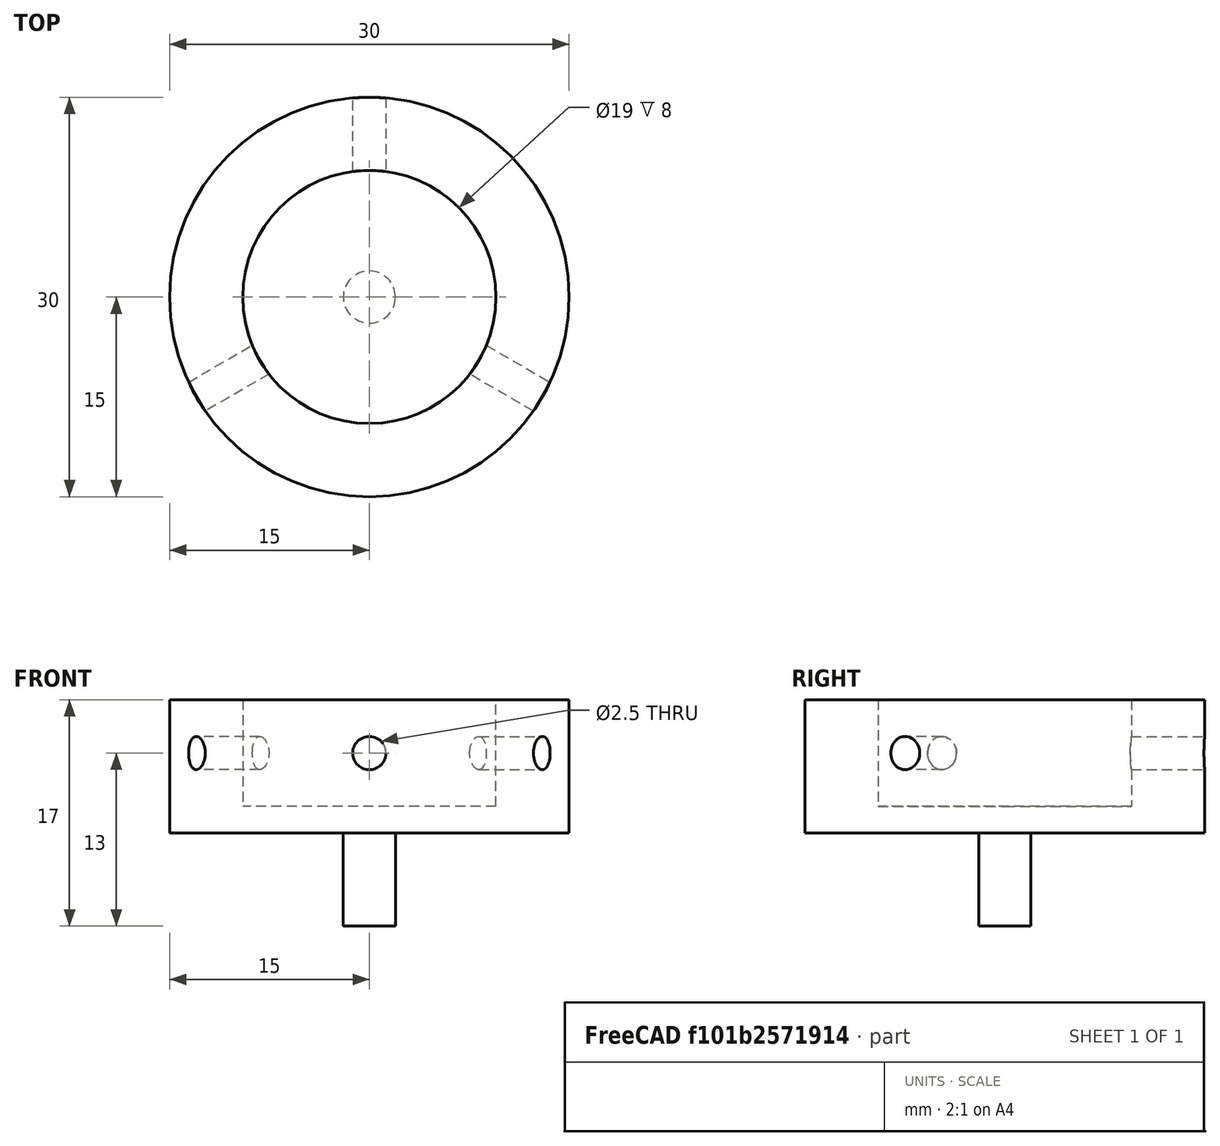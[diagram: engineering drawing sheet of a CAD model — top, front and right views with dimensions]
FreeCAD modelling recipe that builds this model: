
FCSTD DOCUMENT  (FreeCAD 0.20R29603 (Git))
Label: PhilippsXL30_SampleMountAdapter_M4to19mm
License: All rights reserved
LicenseURL: http://en.wikipedia.org/wiki/All_rights_reserved
objects: TechDraw::DrawViewDimension×15, Part::Cylinder×6, TechDraw::DrawProjGroupItem×5, Part::Compound×4, TechDraw::DrawProjGroup×3, Part::Cut×2, TechDraw::DrawViewSection×2, Part::MultiFuse×1, Part::Feature×1, TechDraw::DrawSVGTemplate×1, TechDraw::DrawPage×1
note: 14 computed .brp shape members not serialized (recipe doc carries the construction recipe); baked Part::Feature solids carry a one-line shape summary decoded from their .brp

FEATURE [Part::Cylinder] Cylinder  label="Zylinder"
  Angle = 360
  AttacherType = Attacher::AttachEngine3D
  FirstAngle = 0
  Height = 10
  Radius = 15
  SecondAngle = 0
FEATURE [Part::Cylinder] Cylinder001  label="Zylinder001"
  Angle = 360
  AttacherType = Attacher::AttachEngine3D
  FirstAngle = 0
  Height = 8
  Placement = pos=(0,0,2) rot=(0,0,1;0rad)
  Radius = 9.5
  SecondAngle = 0
FEATURE [Part::Cut] Cut
  Base = -> Cylinder
  Tool = -> Cylinder001
FEATURE [Part::Cylinder] Cylinder002  label="Zylinder002"
  Angle = 360
  AttacherType = Attacher::AttachEngine3D
  FirstAngle = 0
  Height = 6
  Placement = pos=(0,15.2,6) rot=(1,0,0;1.5708rad)
  Radius = 1.25
  SecondAngle = 0
FEATURE [Part::Compound] Compound
  Links = -> [Cylinder002]
FEATURE [Part::Cylinder] Cylinder003  label="Zylinder003"
  Angle = 360
  AttacherType = Attacher::AttachEngine3D
  FirstAngle = 0
  Height = 6
  Placement = pos=(0,15.2,6) rot=(1,0,0;1.5708rad)
  Radius = 1.25
  SecondAngle = 0
FEATURE [Part::Compound] Compound001
  Links = -> [Cylinder003]
  Placement = pos=(0,0,0) rot=(0,0,1;2.0944rad)
FEATURE [Part::Cylinder] Cylinder004  label="Zylinder004"
  Angle = 360
  AttacherType = Attacher::AttachEngine3D
  FirstAngle = 0
  Height = 6
  Placement = pos=(0,15.2,6) rot=(1,0,0;1.5708rad)
  Radius = 1.25
  SecondAngle = 0
FEATURE [Part::Compound] Compound002
  Links = -> [Cylinder004]
  Placement = pos=(0,0,0) rot=(0,0,1;4.18879rad)
FEATURE [Part::Compound] Compound003  label="M3 setscrews"
  Links = -> [Compound,Compound001,Compound002]
FEATURE [Part::Cut] Cut001
  Base = -> Cut
  Tool = -> Compound003
FEATURE [Part::Cylinder] Cylinder005  label="M4 screw"
  Angle = 360
  AttacherType = Attacher::AttachEngine3D
  FirstAngle = 0
  Height = 7
  Placement = pos=(0,0,-7) rot=(0,0,1;0rad)
  Radius = 1.96
  SecondAngle = 0
FEATURE [Part::MultiFuse] Fusion
  Shapes = -> [Cut001,Cylinder005]
FEATURE [Part::Feature] Fusion_solid  label="PhilippsXL30_SampleMountAdapter_M4to19mm"
  shape: bbox 30 x 30 x 17 mm, 10 faces (baked)
FEATURE [TechDraw::DrawSVGTemplate] Template
  EditableTexts = Designed_by_Name=Thomas Spielauer; Drawing_number=1; FC-Date=2023-08-04; FC-SC=mm; FC-SH=1/1; FC-Title=Sample holder Adapter; Subtitle=M4 to 19mm, XL30 ESEM compatible
  Height = 210
  Orientation = 1
  Width = 297
FEATURE [TechDraw::DrawProjGroupItem] ProjItem  label="Top"
  CoarseView = false
  Direction = (0,0,1)
  Focus = 100
  HardHidden = false
  IsoCount = 0
  IsoHidden = false
  IsoVisible = false
  LockPosition = true
  Perspective = false
  Rotation = 0
  RotationVector = (1,0,0)
  ScaleType = 2
  SeamHidden = false
  SeamVisible = true
  SmoothHidden = false
  SmoothVisible = true
  Source = -> [Fusion_solid]
  Type = 0
  X = 0
  XDirection = (1,0,0)
  Y = 0
FEATURE [TechDraw::DrawProjGroupItem] ProjItem003  label="Side"
  CoarseView = false
  Direction = (0,-1,0)
  Focus = 100
  HardHidden = false
  IsoCount = 0
  IsoHidden = false
  IsoVisible = false
  LockPosition = false
  Perspective = false
  Rotation = 0
  RotationVector = (1,0,0)
  ScaleType = 2
  SeamHidden = false
  SeamVisible = true
  SmoothHidden = false
  SmoothVisible = true
  Source = -> [Fusion_solid]
  Type = 5
  X = 0
  XDirection = (1,0,0)
  Y = 52.416
FEATURE [TechDraw::DrawProjGroupItem] ProjItem004  label="Bottom001"
  CoarseView = false
  Direction = (0,0,-1)
  Focus = 100
  HardHidden = false
  IsoCount = 0
  IsoHidden = false
  IsoVisible = false
  LockPosition = false
  Perspective = false
  Rotation = 0
  RotationVector = (1,0,0)
  ScaleType = 2
  SeamHidden = false
  SeamVisible = true
  SmoothHidden = false
  SmoothVisible = true
  Source = -> [Fusion_solid]
  Type = 3
  X = 57.7589
  XDirection = (-1,0,0)
  Y = 0
FEATURE [TechDraw::DrawProjGroup] ProjGroup
  Anchor = -> ProjItem
  AutoDistribute = false
  LockPosition = false
  ProjectionType = 0
  Rotation = 0
  ScaleType = 0
  Source = -> [Fusion_solid]
  Views = -> [ProjItem,ProjItem003,ProjItem004]
  X = 31.0456
  Y = 115.683
  spacingX = 15
  spacingY = 15
FEATURE [TechDraw::DrawViewDimension] Dimension001
  AngleOverride = false
  Arbitrary = false
  ArbitraryTolerances = false
  EqualTolerance = true
  ExtensionAngle = 0
  FormatSpec = %.2w (M4)
  FormatSpecOverTolerance = %+.2w
  FormatSpecUnderTolerance = %+.2w
  Inverted = false
  LineAngle = 0
  LockPosition = false
  MeasureType = 1
  OverTolerance = 0
  References2D = -> [ProjItem003]
  Rotation = 0
  ScaleType = 0
  TheoreticalExact = false
  Type = 0
  UnderTolerance = 0
  X = 14.6767
  Y = -20.2276
FEATURE [TechDraw::DrawViewDimension] Dimension002
  AngleOverride = false
  Arbitrary = false
  ArbitraryTolerances = false
  EqualTolerance = true
  ExtensionAngle = 0
  FormatSpec = %.2w
  FormatSpecOverTolerance = %+.2w
  FormatSpecUnderTolerance = %+.2w
  Inverted = false
  LineAngle = 0
  LockPosition = false
  MeasureType = 1
  OverTolerance = 0
  References2D = -> [ProjItem003]
  Rotation = 0
  ScaleType = 0
  TheoreticalExact = false
  Type = 0
  UnderTolerance = 0
  X = 23.4662
  Y = 14.9409
FEATURE [TechDraw::DrawViewDimension] Dimension003
  AngleOverride = false
  Arbitrary = false
  ArbitraryTolerances = false
  EqualTolerance = true
  ExtensionAngle = 0
  FormatSpec = %.2w
  FormatSpecOverTolerance = %+.2w
  FormatSpecUnderTolerance = %+.2w
  Inverted = false
  LineAngle = 0
  LockPosition = false
  MeasureType = 1
  OverTolerance = 0
  References2D = -> [ProjItem003]
  Rotation = 0
  ScaleType = 0
  TheoreticalExact = false
  Type = 0
  UnderTolerance = 0
  X = 36.9338
  Y = 3.21702
FEATURE [TechDraw::DrawViewDimension] Dimension
  AngleOverride = false
  Arbitrary = false
  ArbitraryTolerances = false
  EqualTolerance = true
  ExtensionAngle = 0
  FormatSpec = ⌀%.2w (M4)
  FormatSpecOverTolerance = %+.2w
  FormatSpecUnderTolerance = %+.2w
  Inverted = false
  LineAngle = 0
  LockPosition = false
  MeasureType = 1
  OverTolerance = 0
  References2D = -> [ProjItem004]
  Rotation = 0
  ScaleType = 0
  TheoreticalExact = false
  Type = 5
  UnderTolerance = 0
  X = 33.2419
  Y = 17.115
FEATURE [TechDraw::DrawViewDimension] Dimension004
  AngleOverride = false
  Arbitrary = false
  ArbitraryTolerances = false
  EqualTolerance = true
  ExtensionAngle = 0
  FormatSpec = ⌀%.2w
  FormatSpecOverTolerance = %+.2w
  FormatSpecUnderTolerance = %+.2w
  Inverted = false
  LineAngle = 0
  LockPosition = false
  MeasureType = 1
  OverTolerance = 0
  References2D = -> [ProjItem004]
  Rotation = 0
  ScaleType = 0
  TheoreticalExact = false
  Type = 5
  UnderTolerance = 0
  X = 39.833
  Y = 7.94479
FEATURE [TechDraw::DrawViewDimension] Dimension005
  AngleOverride = false
  Arbitrary = false
  ArbitraryTolerances = false
  EqualTolerance = true
  ExtensionAngle = 0
  FormatSpec = ⌀%.2w
  FormatSpecOverTolerance = %+.2w
  FormatSpecUnderTolerance = %+.2w
  Inverted = false
  LineAngle = 0
  LockPosition = false
  MeasureType = 1
  OverTolerance = 0
  References2D = -> [ProjItem]
  Rotation = 0
  ScaleType = 0
  TheoreticalExact = false
  Type = 5
  UnderTolerance = 0
  X = 25.9631
  Y = 6.11076
FEATURE [TechDraw::DrawViewDimension] Dimension006
  AngleOverride = false
  Arbitrary = false
  ArbitraryTolerances = false
  EqualTolerance = true
  ExtensionAngle = 0
  FormatSpec = ⌀%.2w
  FormatSpecOverTolerance = %+.2w
  FormatSpecUnderTolerance = %+.2w
  Inverted = false
  LineAngle = 0
  LockPosition = false
  MeasureType = 1
  OverTolerance = 0
  References2D = -> [ProjItem]
  Rotation = 0
  ScaleType = 0
  TheoreticalExact = false
  Type = 5
  UnderTolerance = 0
  X = 21.8365
  Y = 14.7078
FEATURE [TechDraw::DrawProjGroupItem] ProjItem005  label="Side001"
  CoarseView = false
  Direction = (0,-1,0)
  Focus = 100
  HardHidden = false
  IsoCount = 0
  IsoHidden = false
  IsoVisible = false
  LockPosition = true
  Perspective = false
  Rotation = 0
  RotationVector = (1,0,0)
  ScaleType = 2
  SeamHidden = false
  SeamVisible = true
  SmoothHidden = false
  SmoothVisible = true
  Source = -> [Fusion_solid]
  Type = 0
  X = 0
  XDirection = (1,0,0)
  Y = 0
FEATURE [TechDraw::DrawProjGroup] ProjGroup001
  Anchor = -> ProjItem005
  AutoDistribute = false
  LockPosition = false
  ProjectionType = 0
  Rotation = 0
  ScaleType = 2
  Source = -> [Fusion_solid]
  Views = -> [ProjItem005]
  X = 165.246
  Y = 173.103
  spacingX = 15
  spacingY = 15
FEATURE [TechDraw::DrawViewSection] SectionView  label="Section through symmetry axis"
  BaseView = -> ProjItem005
  CoarseView = false
  CutSurfaceDisplay = 2
  Direction = (-1,0,0)
  FileGeomPattern = <path>
  FileHatchPattern = <path>
  Focus = 100
  FuseBeforeCut = false
  HardHidden = false
  HatchScale = 1
  IsoCount = 0
  IsoHidden = false
  IsoVisible = false
  LockPosition = false
  NameGeomPattern = Diamond
  Perspective = false
  Rotation = 0
  Scale = 2
  ScaleType = 2
  SeamHidden = false
  SeamVisible = true
  SectionDirection = 0
  SectionNormal = (-1,0,0)
  SectionOrigin = (0.011,0.003,1.51)
  SmoothHidden = false
  SmoothVisible = true
  Source = -> [Fusion_solid]
  X = 224.837
  XDirection = (0,-1,0)
  Y = 164.034
FEATURE [TechDraw::DrawViewDimension] Dimension007
  AngleOverride = false
  Arbitrary = false
  ArbitraryTolerances = false
  EqualTolerance = true
  ExtensionAngle = 0
  FormatSpec = %.2w
  FormatSpecOverTolerance = %+.2w
  FormatSpecUnderTolerance = %+.2w
  Inverted = false
  LineAngle = 0
  LockPosition = false
  MeasureType = 1
  OverTolerance = 0
  References2D = -> [SectionView]
  Rotation = 0
  ScaleType = 0
  TheoreticalExact = false
  Type = 0
  UnderTolerance = 0
  X = 47.8001
  Y = 13.3627
FEATURE [TechDraw::DrawViewDimension] Dimension008
  AngleOverride = false
  Arbitrary = false
  ArbitraryTolerances = false
  EqualTolerance = true
  ExtensionAngle = 0
  FormatSpec = %.2w
  FormatSpecOverTolerance = %+.2w
  FormatSpecUnderTolerance = %+.2w
  Inverted = false
  LineAngle = 0
  LockPosition = false
  MeasureType = 1
  OverTolerance = 0
  References2D = -> [SectionView]
  Rotation = 0
  ScaleType = 0
  TheoreticalExact = false
  Type = 0
  UnderTolerance = 0
  X = -0.143284
  Y = 31.6791
FEATURE [TechDraw::DrawViewDimension] Dimension009
  AngleOverride = false
  Arbitrary = false
  ArbitraryTolerances = false
  EqualTolerance = true
  ExtensionAngle = 0
  FormatSpec = %.2w
  FormatSpecOverTolerance = %+.2w
  FormatSpecUnderTolerance = %+.2w
  Inverted = false
  LineAngle = 0
  LockPosition = false
  MeasureType = 1
  OverTolerance = 0
  References2D = -> [SectionView]
  Rotation = 0
  ScaleType = 0
  TheoreticalExact = false
  Type = 0
  UnderTolerance = 0
  X = 0.429852
  Y = -31.7359
FEATURE [TechDraw::DrawViewDimension] Dimension010
  AngleOverride = false
  Arbitrary = false
  ArbitraryTolerances = false
  EqualTolerance = true
  ExtensionAngle = 0
  FormatSpec = %.2w
  FormatSpecOverTolerance = %+.2w
  FormatSpecUnderTolerance = %+.2w
  Inverted = false
  LineAngle = 0
  LockPosition = false
  MeasureType = 1
  OverTolerance = 0
  References2D = -> [SectionView]
  Rotation = 0
  ScaleType = 0
  TheoreticalExact = false
  Type = 0
  UnderTolerance = 0
  X = 48.338
  Y = -6.49701
FEATURE [TechDraw::DrawViewDimension] Dimension011
  AngleOverride = false
  Arbitrary = false
  ArbitraryTolerances = false
  EqualTolerance = true
  ExtensionAngle = 0
  FormatSpec = %.2w
  FormatSpecOverTolerance = %+.2w
  FormatSpecUnderTolerance = %+.2w
  Inverted = false
  LineAngle = 0
  LockPosition = false
  MeasureType = 1
  OverTolerance = 0
  References2D = -> [SectionView]
  Rotation = 0
  ScaleType = 0
  TheoreticalExact = false
  Type = 0
  UnderTolerance = 0
  X = 59.8927
  Y = 3.93284
FEATURE [TechDraw::DrawViewDimension] Dimension012
  AngleOverride = false
  Arbitrary = false
  ArbitraryTolerances = false
  EqualTolerance = true
  ExtensionAngle = 0
  FormatSpec = %.2w
  FormatSpecOverTolerance = %+.2w
  FormatSpecUnderTolerance = %+.2w
  Inverted = false
  LineAngle = 0
  LockPosition = false
  MeasureType = 1
  OverTolerance = 0
  References2D = -> [SectionView]
  Rotation = 0
  ScaleType = 0
  TheoreticalExact = false
  Type = 0
  UnderTolerance = 0
  X = -30.1194
  Y = 29.7649
FEATURE [TechDraw::DrawViewDimension] Dimension013
  AngleOverride = false
  Arbitrary = false
  ArbitraryTolerances = false
  EqualTolerance = true
  ExtensionAngle = 0
  FormatSpec = ⌀%.2w (3x M3)
  FormatSpecOverTolerance = %+.2w
  FormatSpecUnderTolerance = %+.2w
  Inverted = false
  LineAngle = 0
  LockPosition = false
  MeasureType = 1
  OverTolerance = 0
  References2D = -> [ProjItem003]
  Rotation = 0
  ScaleType = 0
  TheoreticalExact = false
  Type = 5
  UnderTolerance = 0
  X = 13.7288
  Y = 22.3335
FEATURE [TechDraw::DrawProjGroupItem] ProjItem006  label="Side002"
  CoarseView = false
  Direction = (0,-1,0)
  Focus = 100
  HardHidden = false
  IsoCount = 0
  IsoHidden = false
  IsoVisible = false
  LockPosition = true
  Perspective = false
  Rotation = 0
  RotationVector = (1,0,0)
  ScaleType = 2
  SeamHidden = false
  SeamVisible = true
  SmoothHidden = false
  SmoothVisible = true
  Source = -> [Fusion_solid]
  Type = 0
  X = 0
  XDirection = (1,0,0)
  Y = 0
FEATURE [TechDraw::DrawProjGroup] ProjGroup002
  Anchor = -> ProjItem006
  AutoDistribute = false
  LockPosition = false
  ProjectionType = 0
  Rotation = 0
  ScaleType = 0
  Source = -> [Fusion_solid]
  Views = -> [ProjItem006]
  X = 44.2188
  Y = 30.7924
  spacingX = 15
  spacingY = 15
FEATURE [TechDraw::DrawViewSection] SectionView001  label="Horizontal section"
  BaseView = -> ProjItem006
  CoarseView = false
  CutSurfaceDisplay = 2
  Direction = (0,0,1)
  FileGeomPattern = <path>
  FileHatchPattern = <path>
  Focus = 100
  FuseBeforeCut = false
  HardHidden = false
  HatchScale = 1
  IsoCount = 0
  IsoHidden = false
  IsoVisible = false
  LockPosition = false
  NameGeomPattern = Diamond
  Perspective = false
  Rotation = 0
  ScaleType = 2
  SeamHidden = false
  SeamVisible = true
  SectionDirection = 3
  SectionNormal = (0,0,1)
  SectionOrigin = (0.011,0.003,6)
  SmoothHidden = false
  SmoothVisible = true
  Source = -> [Fusion_solid]
  X = 98.5075
  XDirection = (1,0,0)
  Y = 35.8698
FEATURE [TechDraw::DrawViewDimension] Dimension014
  AngleOverride = false
  Arbitrary = false
  ArbitraryTolerances = false
  EqualTolerance = true
  ExtensionAngle = 0
  FormatSpec = %.2w
  FormatSpecOverTolerance = %+.2w
  FormatSpecUnderTolerance = %+.2w
  Inverted = false
  LineAngle = 0
  LockPosition = false
  MeasureType = 1
  OverTolerance = 0
  References2D = -> [SectionView001]
  Rotation = 0
  ScaleType = 0
  TheoreticalExact = false
  Type = 6
  UnderTolerance = 0
  X = 22.7083
  Y = 14.8966
FEATURE [TechDraw::DrawPage] Page
  KeepUpdated = true
  NextBalloonIndex = 1
  ProjectionType = 0
  Template = -> Template
  Views = -> [ProjGroup,Dimension001,Dimension002,Dimension003,Dimension,Dimension004,Dimension005,Dimension006,ProjGroup001,SectionView,Dimension007,Dimension008,Dimension009,Dimension010,Dimension011,Dimension012,Dimension013,ProjGroup002,SectionView001,Dimension014]
note: 4 file-system paths scrubbed to <path> (originals preserved in the JSON sidecar)
